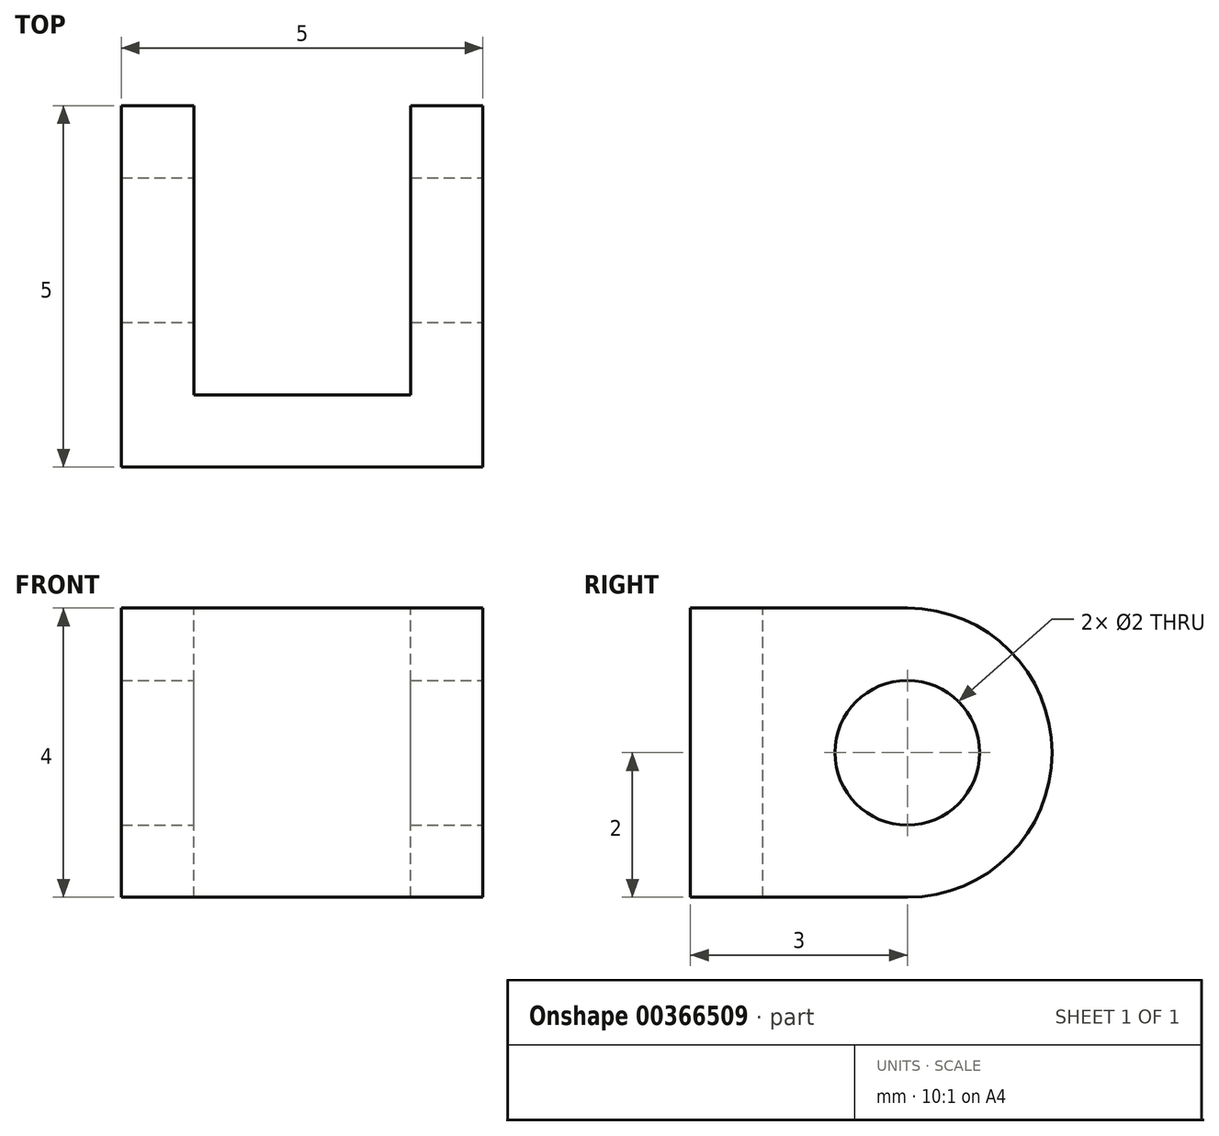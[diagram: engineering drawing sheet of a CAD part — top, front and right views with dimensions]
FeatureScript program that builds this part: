
annotation { "Feature Type Name" : "Feature", "Feature Type Description" : "" }
export const myFeature = defineFeature(function(context is Context, id is Id, definition is map)
    precondition{}
    {
        {
            var Q0;
            Q0=qCreatedBy(makeId("Top.planeOp"),FACE);
            var sketch = newSketch(context, id + "F0", { "sketchPlane" : qUnion([Q0])});
            skLineSegment(sketch, "E0", {"start": v(0, 0) * mm, "end": v(5, 0) * mm});
            skLineSegment(sketch, "E1", {"start": v(5, 0) * mm, "end": v(5, 5) * mm});
            skLineSegment(sketch, "E2", {"start": v(5, 5) * mm, "end": v(0, 5) * mm});
            skLineSegment(sketch, "E3", {"start": v(0, 5) * mm, "end": v(0, 0) * mm});
            skSolve(sketch);
        }
        {
            var Q0;
            Q0=qSketchRegion(id+"F0",true);
            extrude(context, id + "F1", {"entities" : qUnion([Q0]), "depth" : 4 * mm});
        }
        {
            var Q0;
            Q0=makeQuery(id+"F1.opExtrude","SWEPT_FACE",FACE,{"disambiguationData":[OSD([sQuery(id+"F0.wireOp",EDGE,"E1")])]});
            var sketch = newSketch(context, id + "F2", { "sketchPlane" : qUnion([Q0])});
            skLineSegment(sketch, "E4", {"start": v(0, 4) * mm, "end": v(3, 4) * mm});
            skLineSegment(sketch, "E5", {"start": v(3, 4) * mm, "end": v(3, 2) * mm});
            skCircle(sketch, "E6", {"center": v(3, 2) * mm, "radius": 2 * mm});
            skSolve(sketch);
        }
        {
            var Q0;
            {var subQ0=sQuery(id+"F2.wireOp",EDGE,"E6");var subQ1=sQuery(id+"F0.wireOp",EDGE,"E1");var subQ2=makeQuery(id+"F1.opExtrude","CAP_EDGE",EDGE,{"disambiguationData":[OSD([subQ1])],"isStart":false});var subQ3=makeQuery(id+"F2.imprint","INTERSECT",VERTEX,{"derivedFrom":[subQ2,sQuery(id+"F2.wireOp",EDGE,"E4"),subQ0]});Q0=makeQuery(id+"F2.imprint","IMPRINT",FACE,{"disambiguationData":[TD([[makeQuery(id+"F2.imprint","IMPRINT",EDGE,{"disambiguationData":[TD([[subQ3,1.0]])],"derivedFrom":subQ0}),-1.0]])]});}
            var Q1;
            {var subQ0=sQuery(id+"F2.wireOp",EDGE,"E6");var subQ1=sQuery(id+"F0.wireOp",EDGE,"E1");var subQ4=makeQuery(id+"F1.opExtrude","CAP_EDGE",EDGE,{"disambiguationData":[OSD([subQ1])],"isStart":true});var subQ5=makeQuery(id+"F2.imprint","INTERSECT",VERTEX,{"derivedFrom":[subQ4,subQ0]});Q1=makeQuery(id+"F2.imprint","IMPRINT",FACE,{"disambiguationData":[TD([[makeQuery(id+"F2.imprint","IMPRINT",EDGE,{"disambiguationData":[TD([[subQ5,-1.0]])],"derivedFrom":subQ0}),-1.0]])]});}
            extrude(context, id + "F3", {"entities" : qUnion([Q0, Q1]), "operationType" : NewBodyOperationType.REMOVE, "oppositeDirection" : true, "depth" : 25 * mm});
        }
        {
            var Q0;
            Q0=makeQuery(id+"F1.opExtrude","CAP_FACE",FACE,{"disambiguationData":[OSD([sQuery(id+"F0.wireOp",EDGE,"E0"),sQuery(id+"F0.wireOp",EDGE,"E1"),sQuery(id+"F0.wireOp",EDGE,"E2"),sQuery(id+"F0.wireOp",EDGE,"E3")])],"isStart":false});
            var sketch = newSketch(context, id + "F4", { "sketchPlane" : qUnion([Q0])});
            skLineSegment(sketch, "E7", {"start": v(0, 0) * mm, "end": v(1, 0) * mm});
            skLineSegment(sketch, "E8", {"start": v(1, 0) * mm, "end": v(1, 1) * mm});
            skLineSegment(sketch, "E9", {"start": v(1, 1) * mm, "end": v(1, 5) * mm});
            skLineSegment(sketch, "E10", {"start": v(1, 1) * mm, "end": v(4, 1) * mm});
            skLineSegment(sketch, "E11", {"start": v(4, 1) * mm, "end": v(4, 5) * mm});
            skSolve(sketch);
        }
        {
            var Q0;
            {var subQ0=sQuery(id+"F4.wireOp",EDGE,"E10");Q0=makeQuery(id+"F4.imprint","IMPRINT",FACE,{"disambiguationData":[TD([[makeQuery(id+"F4.imprint","IMPRINT",EDGE,{"derivedFrom":subQ0}),1.0]])]});}
            extrude(context, id + "F5", {"entities" : qUnion([Q0]), "operationType" : NewBodyOperationType.REMOVE, "oppositeDirection" : true, "depth" : 5 * mm});
        }
        {
            var Q0;
            Q0=makeQuery(id+"F1.opExtrude","CAP_FACE",FACE,{"disambiguationData":[OSD([sQuery(id+"F0.wireOp",EDGE,"E0"),sQuery(id+"F0.wireOp",EDGE,"E1"),sQuery(id+"F0.wireOp",EDGE,"E2"),sQuery(id+"F0.wireOp",EDGE,"E3")])],"isStart":false});
            var sketch = newSketch(context, id + "F6", { "sketchPlane" : qUnion([Q0])});
            skLineSegment(sketch, "E12", {"start": v(1, 3) * mm, "end": v(1, 5) * mm});
            skLineSegment(sketch, "E13", {"start": v(4, 3) * mm, "end": v(4, 5) * mm});
            skLineSegment(sketch, "E14", {"start": v(1, 5) * mm, "end": v(4, 5) * mm});
            skLineSegment(sketch, "E15", {"start": v(1, 3) * mm, "end": v(4, 3) * mm});
            skSolve(sketch);
        }
        {
            var Q0;
            Q0=makeQuery(id+"F6.imprint","IMPRINT",FACE,{"disambiguationData":[TD([[makeQuery(id+"F6.imprint","IMPRINT",EDGE,{"derivedFrom":sQuery(id+"F6.wireOp",EDGE,"E12")}),-1.0]])]});
            extrude(context, id + "F7", {"entities" : qUnion([Q0]), "operationType" : NewBodyOperationType.REMOVE, "oppositeDirection" : true, "depth" : 5 * mm});
        }
        {
            var Q0;
            Q0=makeQuery(id+"F1.opExtrude","SWEPT_FACE",FACE,{"disambiguationData":[OSD([sQuery(id+"F0.wireOp",EDGE,"E1")])]});
            var sketch = newSketch(context, id + "F8", { "sketchPlane" : qUnion([Q0])});
            skLineSegment(sketch, "E16", {"start": v(0, 4) * mm, "end": v(0, 2) * mm});
            skLineSegment(sketch, "E17", {"start": v(0, 2) * mm, "end": v(3, 2) * mm});
            skCircle(sketch, "E18", {"center": v(3, 2) * mm, "radius": 1 * mm});
            skSolve(sketch);
        }
        {
            var Q0;
            Q0=makeQuery(id+"F8.imprint","IMPRINT",FACE,{"disambiguationData":[TD([[makeQuery(id+"F8.imprint","IMPRINT",EDGE,{"derivedFrom":sQuery(id+"F8.wireOp",EDGE,"E18")}),1.0]])]});
            extrude(context, id + "F9", {"entities" : qUnion([Q0]), "operationType" : NewBodyOperationType.REMOVE, "oppositeDirection" : true, "depth" : 25 * mm});
        }
    });
